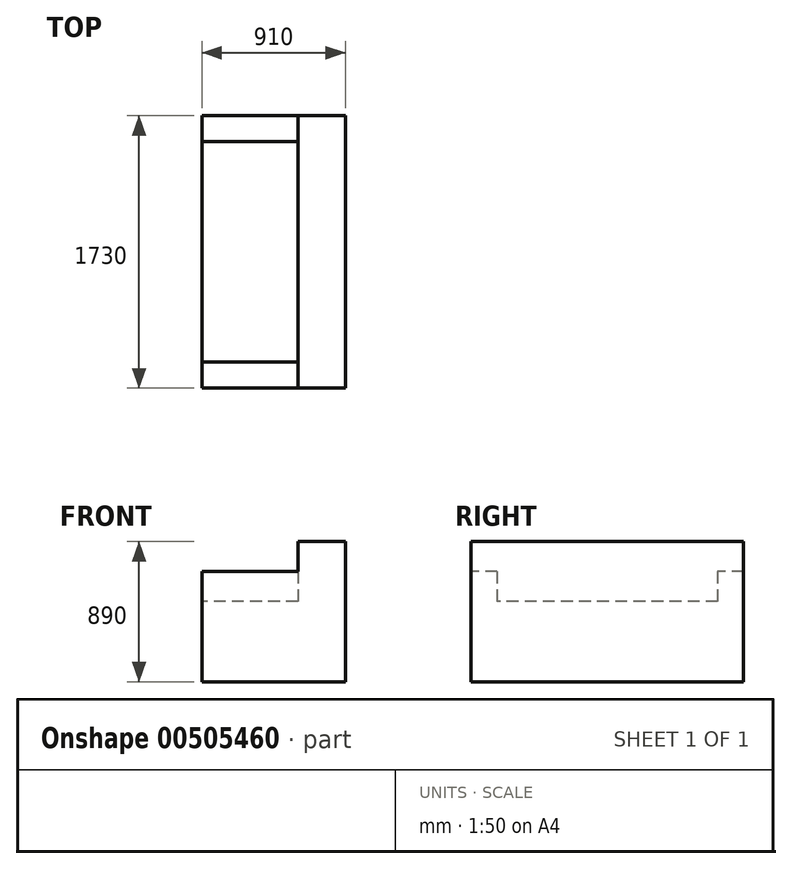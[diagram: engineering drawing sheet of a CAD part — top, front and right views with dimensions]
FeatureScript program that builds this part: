
annotation { "Feature Type Name" : "Feature", "Feature Type Description" : "" }
export const myFeature = defineFeature(function(context is Context, id is Id, definition is map)
    precondition{}
    {
        {
            var Q0;
            Q0=qCreatedBy(makeId("Top.planeOp"),FACE);
            var sketch = newSketch(context, id + "F0", { "sketchPlane" : qUnion([Q0])});
            skLineSegment(sketch, "E0.bottom", {"start": v(465.5, 865) * mm, "end": v(-444.5, 865) * mm});
            skLineSegment(sketch, "E0.top", {"start": v(465.5, -865) * mm, "end": v(-444.5, -865) * mm});
            skLineSegment(sketch, "E0.left", {"start": v(465.5, 865) * mm, "end": v(465.5, -865) * mm});
            skLineSegment(sketch, "E0.right", {"start": v(-444.5, 865) * mm, "end": v(-444.5, -865) * mm});
            skPoint(sketch, "E0.middle", {"position": v(10.5, 0) * mm});
            skSolve(sketch);
        }
        {
            var Q0;
            Q0=qSketchRegion(id+"F0",true);
            extrude(context, id + "F1", {"entities" : qUnion([Q0]), "depth" : 890 * mm});
        }
        {
            var Q0;
            Q0=makeQuery(id+"F1.opExtrude","SWEPT_FACE",FACE,{"disambiguationData":[OSD([sQuery(id+"F0.wireOp",EDGE,"E0.right")])]});
            var sketch = newSketch(context, id + "F2", { "sketchPlane" : qUnion([Q0])});
            skLineSegment(sketch, "E1.bottom", {"start": v(-700, 890) * mm, "end": v(700, 890) * mm});
            skLineSegment(sketch, "E1.top", {"start": v(-700, 510) * mm, "end": v(700, 510) * mm});
            skLineSegment(sketch, "E1.left", {"start": v(-700, 890) * mm, "end": v(-700, 510) * mm});
            skLineSegment(sketch, "E1.right", {"start": v(700, 890) * mm, "end": v(700, 510) * mm});
            skLineSegment(sketch, "E2", {"start": v(0, 890) * mm, "end": v(0, 510) * mm, "construction": true});
            skSolve(sketch);
        }
        {
            var Q0;
            Q0=qSketchRegion(id+"F2",true);
            extrude(context, id + "F3", {"entities" : qUnion([Q0]), "operationType" : NewBodyOperationType.REMOVE, "oppositeDirection" : true, "depth" : 610 * mm});
        }
        {
            var Q0;
            Q0=makeQuery(id+"F1.opExtrude","SWEPT_FACE",FACE,{"disambiguationData":[OSD([sQuery(id+"F0.wireOp",EDGE,"E0.right")])]});
            var sketch = newSketch(context, id + "F4", { "sketchPlane" : qUnion([Q0])});
            skLineSegment(sketch, "E3.bottom", {"start": v(-865, 890) * mm, "end": v(-700, 890) * mm});
            skLineSegment(sketch, "E3.top", {"start": v(-865, 700) * mm, "end": v(-700, 700) * mm});
            skLineSegment(sketch, "E3.left", {"start": v(-865, 890) * mm, "end": v(-865, 700) * mm});
            skLineSegment(sketch, "E3.right", {"start": v(-700, 890) * mm, "end": v(-700, 700) * mm});
            skLineSegment(sketch, "E4.bottom", {"start": v(700, 890) * mm, "end": v(865, 890) * mm});
            skLineSegment(sketch, "E4.top", {"start": v(700, 700) * mm, "end": v(865, 700) * mm});
            skLineSegment(sketch, "E4.left", {"start": v(700, 890) * mm, "end": v(700, 700) * mm});
            skLineSegment(sketch, "E4.right", {"start": v(865, 890) * mm, "end": v(865, 700) * mm});
            skSolve(sketch);
        }
        {
            var Q0;
            Q0 = qSketchRegion(id + "F4", true);
            var Q1;
            Q1=makeQuery(id+"F3.boolean.opBoolean","COPY",FACE,{"derivedFrom":makeQuery(id+"F3.opExtrude","CAP_FACE",FACE,{"disambiguationData":[OSD([sQuery(id+"F2.wireOp",EDGE,"E1.bottom"),sQuery(id+"F2.wireOp",EDGE,"E1.top"),sQuery(id+"F2.wireOp",EDGE,"E1.left"),sQuery(id+"F2.wireOp",EDGE,"E1.right")])],"isStart":false})});
            extrude(context, id + "F5", {"entities" : qUnion([Q0]), "operationType" : NewBodyOperationType.REMOVE, "endBound" : BoundingType.UP_TO_SURFACE, "oppositeDirection" : true, "endBoundEntityFace" : qUnion([Q1]), "depth" : 25 * mm});
        }
    });
